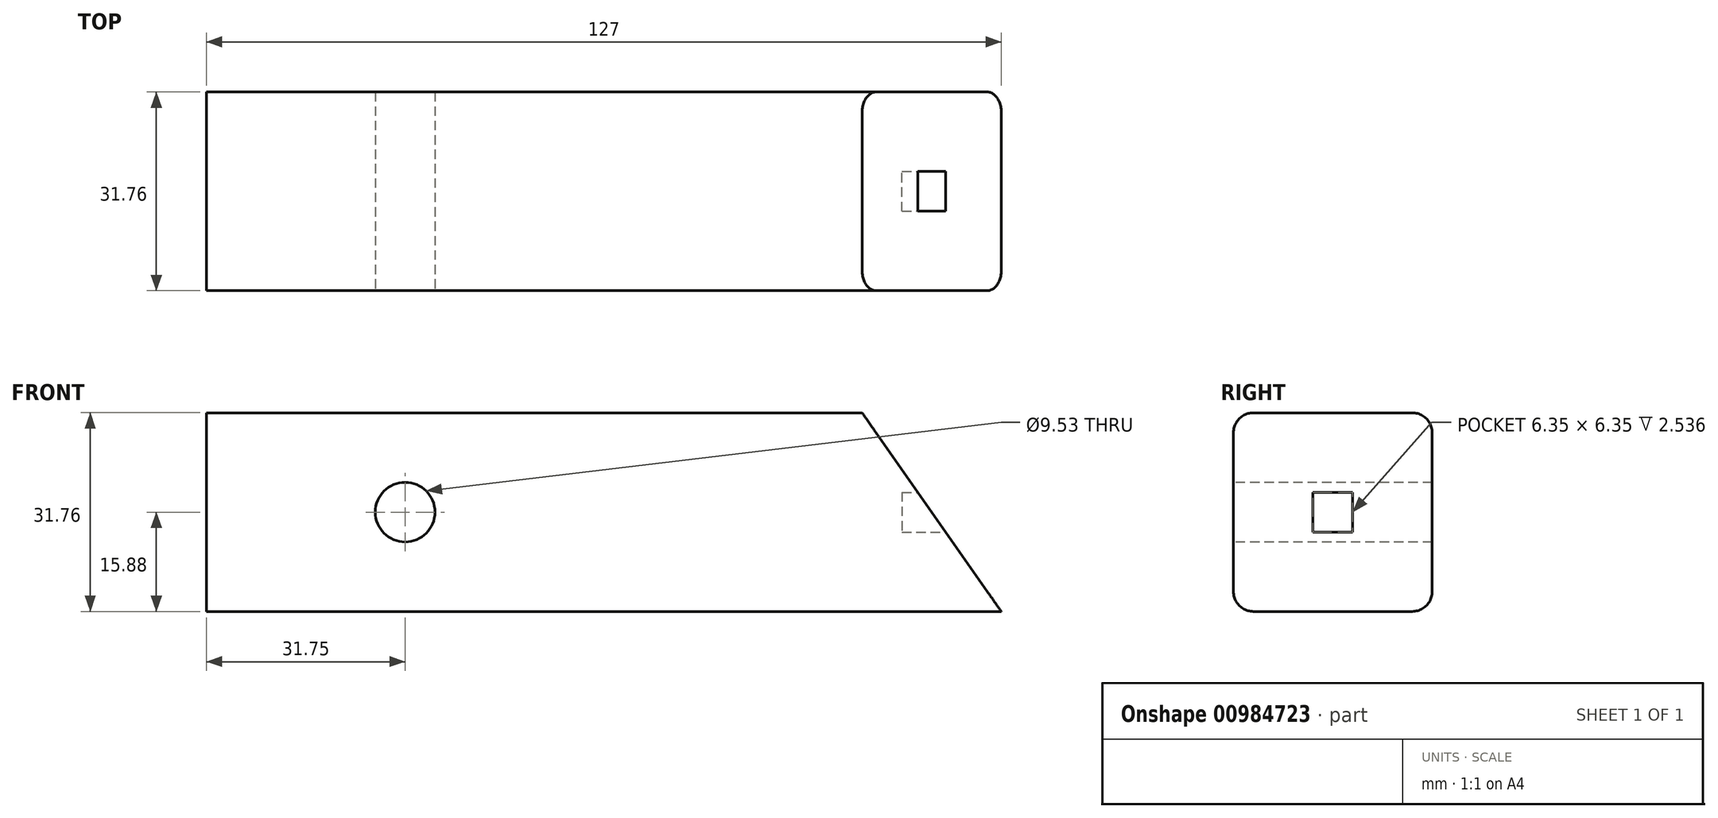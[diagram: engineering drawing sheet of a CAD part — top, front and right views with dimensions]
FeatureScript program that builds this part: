
annotation { "Feature Type Name" : "Feature", "Feature Type Description" : "" }
export const myFeature = defineFeature(function(context is Context, id is Id, definition is map)
    precondition{}
    {
        {
            var Q0;
            Q0=qCreatedBy(makeId("Front.planeOp"),FACE);
            var sketch = newSketch(context, id + "F0", { "sketchPlane" : qUnion([Q0])});
            skLineSegment(sketch, "E0.bottom", {"start": v(-63.5, 15.88) * mm, "end": v(63.5, 15.88) * mm});
            skLineSegment(sketch, "E0.top", {"start": v(-63.5, -15.87) * mm, "end": v(63.5, -15.87) * mm});
            skLineSegment(sketch, "E0.left", {"start": v(-63.5, 15.88) * mm, "end": v(-63.5, -15.87) * mm});
            skLineSegment(sketch, "E0.right", {"start": v(63.5, 15.88) * mm, "end": v(63.5, -15.87) * mm});
            skPoint(sketch, "E0.middle", {"position": v(0, 0) * mm});
            skSolve(sketch);
        }
        {
            var Q0;
            Q0 = qSketchRegion(id + "F0", true);
            extrude(context, id + "F1", {"entities" : qUnion([Q0]), "depth" : 31.75 * mm, "offsetDistance" : 25.4 * mm, "symmetric" : true});
        }
        {
            var Q0;
            Q0=makeQuery(id+"F1.opExtrude","CAP_FACE",FACE,{"disambiguationData":[OSD([sQuery(id+"F0.wireOp",EDGE,"E0.bottom"),sQuery(id+"F0.wireOp",EDGE,"E0.top"),sQuery(id+"F0.wireOp",EDGE,"E0.left"),sQuery(id+"F0.wireOp",EDGE,"E0.right")])],"isStart":false});
            var sketch = newSketch(context, id + "F2", { "sketchPlane" : qUnion([Q0])});
            skCircle(sketch, "E1", {"center": v(-31.75, 0) * mm, "radius": 4.76 * mm});
            skSolve(sketch);
        }
        {
            var Q0;
            Q0 = qSketchRegion(id + "F2", true);
            extrude(context, id + "F3", {"entities" : qUnion([Q0]), "operationType" : NewBodyOperationType.REMOVE, "endBound" : BoundingType.THROUGH_ALL, "oppositeDirection" : true, "depth" : 25.4 * mm, "offsetDistance" : 25.4 * mm});
        }
        {
            var Q0;
            Q0=makeQuery(id+"F1.opExtrude","CAP_FACE",FACE,{"disambiguationData":[OSD([sQuery(id+"F0.wireOp",EDGE,"E0.bottom"),sQuery(id+"F0.wireOp",EDGE,"E0.top"),sQuery(id+"F0.wireOp",EDGE,"E0.left"),sQuery(id+"F0.wireOp",EDGE,"E0.right")])],"isStart":false});
            var sketch = newSketch(context, id + "F4", { "sketchPlane" : qUnion([Q0])});
            skLineSegment(sketch, "E2", {"start": v(63.5, -15.87) * mm, "end": v(41.27, 15.88) * mm});
            skSolve(sketch);
        }
        {
            var Q0;
            {var subQ0=sQuery(id+"F4.wireOp",EDGE,"E2");Q0=makeQuery(id+"F4.imprint","IMPRINT",FACE,{"disambiguationData":[TD([[makeQuery(id+"F4.imprint","IMPRINT",EDGE,{"derivedFrom":subQ0}),-1.0]])]});}
            extrude(context, id + "F5", {"entities" : qUnion([Q0]), "operationType" : NewBodyOperationType.REMOVE, "endBound" : BoundingType.THROUGH_ALL, "oppositeDirection" : true, "depth" : 25.4 * mm, "offsetDistance" : 25.4 * mm});
        }
        {
            var Q0;
            Q0=qCreatedBy(makeId("Right.planeOp"),FACE);
            cPlane(context, id + "F6", {"entities" : qUnion([Q0]), "cplaneType" : CPlaneType.OFFSET, "offset" : 63.5 * mm, "width" : 152.4 * mm, "height" : 152.4 * mm});
        }
        {
            var Q0;
            Q0=qCreatedBy(id+"F6.planeOp",FACE);
            var sketch = newSketch(context, id + "F7", { "sketchPlane" : qUnion([Q0])});
            skLineSegment(sketch, "E3.bottom", {"start": v(-3.17, 3.18) * mm, "end": v(3.18, 3.18) * mm});
            skLineSegment(sketch, "E3.top", {"start": v(-3.18, -3.18) * mm, "end": v(3.17, -3.18) * mm});
            skLineSegment(sketch, "E3.left", {"start": v(-3.17, 3.18) * mm, "end": v(-3.18, -3.18) * mm});
            skLineSegment(sketch, "E3.right", {"start": v(3.18, 3.18) * mm, "end": v(3.17, -3.18) * mm});
            skPoint(sketch, "E3.middle", {"position": v(0, 0) * mm});
            skSolve(sketch);
        }
        {
            var Q0;
            Q0 = qSketchRegion(id + "F7", true);
            extrude(context, id + "F8", {"entities" : qUnion([Q0]), "operationType" : NewBodyOperationType.REMOVE, "oppositeDirection" : true, "depth" : 15.88 * mm, "offsetDistance" : 25.4 * mm});
        }
        {
            var Q0;
            Q0=makeQuery(id+"F1.opExtrude","CAP_EDGE",EDGE,{"disambiguationData":[OSD([sQuery(id+"F0.wireOp",EDGE,"E0.bottom")])],"isStart":false});
            var Q1;
            Q1=makeQuery(id+"F1.opExtrude","CAP_EDGE",EDGE,{"disambiguationData":[OSD([sQuery(id+"F0.wireOp",EDGE,"E0.bottom")])],"isStart":true});
            var Q2;
            Q2=makeQuery(id+"F1.opExtrude","CAP_EDGE",EDGE,{"disambiguationData":[OSD([sQuery(id+"F0.wireOp",EDGE,"E0.top")])],"isStart":false});
            var Q3;
            Q3=makeQuery(id+"F1.opExtrude","CAP_EDGE",EDGE,{"disambiguationData":[OSD([sQuery(id+"F0.wireOp",EDGE,"E0.top")])],"isStart":true});
            fillet(context, id + "F9", {"entities" : qUnion([Q0, Q1, Q2, Q3]), "radius" : 3.17 * mm, "tangentPropagation" : true, "allowEdgeOverflow" : false});
        }
    });
